# Revit family: ledbollard-p1-_l600-10_5w-4000-w_543012002900_fe1b
name_source: partatom
category: Leuchten
revit_build: Autodesk Revit 2016 (Build: 20190508_0715(x64)
units: mm (PartAtom-declared; Revit-internal decimal feet)

## family parameters
Basisbauteil = Fläche
Beim Laden mit Abzugskörper schneiden = Nein
Bemaßung runder Anschluss = Durchmesser verwenden
Gemeinsam genutzt = Nein
Lichtquelle = Nein
Raumberechnungspunkt = Nein
Teiletyp = Normal

## types (1)
- LEDBollard-P1- L600-10.5W-4000-W (1 x LED, 1000 lm)
    Approval mark = CE, ENEC
    Beschreibung = Professional urban landscape luminaire with discreet design. Special optics to reduce glare to pedestrians. Die casted aluminium body for optimal heat dissipation. Safe installation thanks to the included anti vandal screws. Easy to install thanks to its ground plate threaded design. Suitable for use on the coastal applications.
    CIE Flux Codes = 15 44 74 63 100
    Control Gear = Electronic ballast
    Height = 0 mm  [stored 0 ft]
    Hersteller = OPPLE
    Lamp Light Flux = 1000 lm
    Lamp count = 1
    Lampe = 1 x LED
    Length = 160 mm
    Luminous efficacy = 95 lm/W
    ModVariant = Nein
    Modell = 543012002900
    Mounting Place = Floor
    Mounting Type = Surface mounted
    Number of Poles = 1
    OnlyDefault = Ja
    Power Factor = 1
    Product Name = LEDBollard-P1- L600-10.5W-4000-W
    Product group = Bollard
    ProductGroupID = 3301
    Protection Class = Protection class I
    Protection Degree = IP 65
    RLX_Detail_Level = 1
    RlxData = <blob elided: 96705 chars, md5=dec91492>
    Scheinlast = 11 VA
    Socket = socket
    Standby Power = 0 W
    System Light Flux = 1000 lm
    System Power = 11 W
    Typenbild = boll.jpg
    Typenkommentare = Product without accessories
    URL = http://relux.com
    VarID = ---
    Voltage = 0 V
    Vorgabe-Ansicht = 1800 mm
    Weight = 0.00 kg
    Width = 0 mm  [stored 0 ft]

note: [stored X ft] marks values corroborated as IEEE doubles in the binary element streams (Revit-internal decimal feet)

## geometry (parser evidence)
native form markers: Blend x4, Sweep x14
no freeform markers — native parametric forms only
